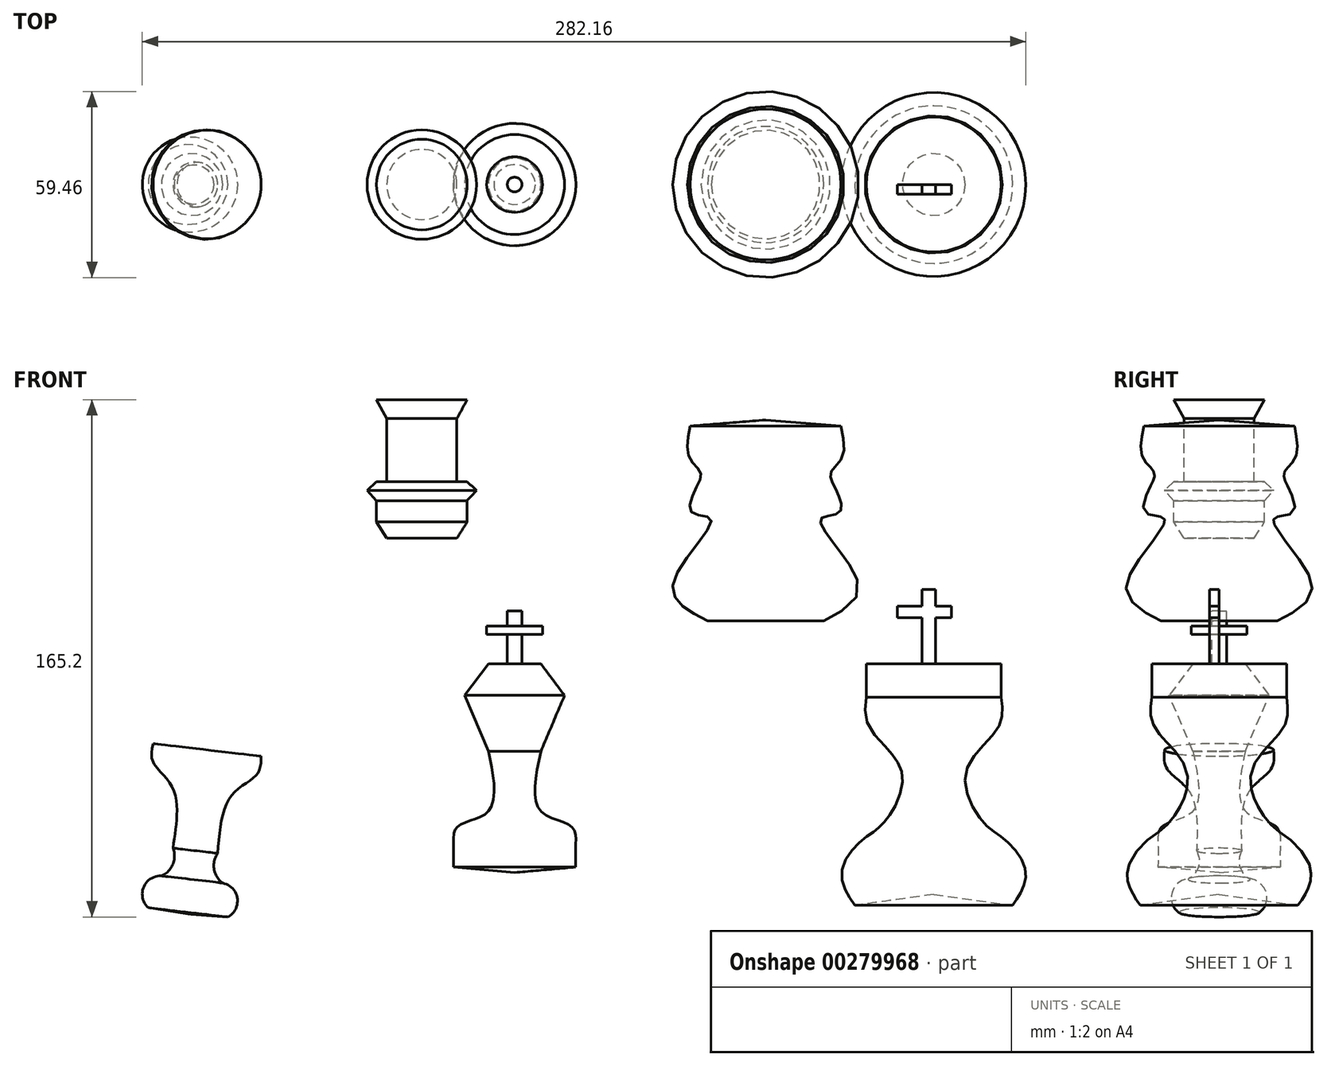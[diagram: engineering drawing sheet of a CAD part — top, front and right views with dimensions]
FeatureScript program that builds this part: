
annotation { "Feature Type Name" : "Feature", "Feature Type Description" : "" }
export const myFeature = defineFeature(function(context is Context, id is Id, definition is map)
    precondition{}
    {
        {
            var Q0;
            Q0=qCreatedBy(makeId("Front.planeOp"),FACE);
            var sketch = newSketch(context, id + "F0", { "sketchPlane" : qUnion([Q0])});
            skFitSpline(sketch, "E0", {"points": [v(-36.24, -64.9) * mm, v(-36.24, -57.78) * mm, v(-34.9, -51.99) * mm, v(-25.1, -47.08) * mm, v(-25.1, -27.92) * mm], "startDerivative": vector(0.5, 34) * mm, "endDerivative": vector(-14.24, 68.29) * mm});
            skLineSegment(sketch, "E1", {"start": v(-25.1, -27.92) * mm, "end": v(-32.67, -10.1) * mm});
            skLineSegment(sketch, "E2", {"start": v(-32.67, -10.1) * mm, "end": v(-25.1, 0) * mm});
            skLineSegment(sketch, "E3", {"start": v(-25.1, 0) * mm, "end": v(-16.72, 0) * mm});
            skLineSegment(sketch, "E4", {"start": v(-16.72, 0) * mm, "end": v(-16.72, -66.68) * mm});
            skLineSegment(sketch, "E5", {"start": v(-16.72, -66.68) * mm, "end": v(-36.2, -62.54) * mm});
            skLineSegment(sketch, "E6", {"start": v(-36.24, -64.9) * mm, "end": v(-16.72, -66.68) * mm});
            skLineSegment(sketch, "E7", {"start": v(-19.06, 0) * mm, "end": v(-19.06, 9.43) * mm});
            skLineSegment(sketch, "E8", {"start": v(-19.06, 9.43) * mm, "end": v(-25.62, 9.43) * mm});
            skLineSegment(sketch, "E9", {"start": v(-25.62, 9.43) * mm, "end": v(-25.62, 12.06) * mm});
            skLineSegment(sketch, "E10", {"start": v(-25.62, 12.06) * mm, "end": v(-19.06, 12.06) * mm});
            skLineSegment(sketch, "E11", {"start": v(-19.06, 12.06) * mm, "end": v(-19.06, 16.83) * mm});
            skLineSegment(sketch, "E12", {"start": v(-16.72, 0) * mm, "end": v(-16.72, 16.93) * mm});
            skLineSegment(sketch, "E13", {"start": v(-16.72, 16.93) * mm, "end": v(-19.06, 16.83) * mm});
            skSolve(sketch);
        }
        {
            var Q0;
            Q0=makeQuery(id+"F0.imprint","IMPRINT",FACE,{"disambiguationData":[TD([[makeQuery(id+"F0.imprint","IMPRINT",EDGE,{"derivedFrom":sQuery(id+"F0.wireOp",EDGE,"E0")}),-1.0]])]});
            var Q1;
            {var subQ0=sQuery(id+"F0.wireOp",EDGE,"E7");Q1=makeQuery(id+"F0.imprint","IMPRINT",FACE,{"disambiguationData":[TD([[makeQuery(id+"F0.imprint","IMPRINT",EDGE,{"derivedFrom":subQ0}),-1.0]])]});}
            var Q2;
            Q2=sQuery(id+"F0.wireOp",EDGE,"E4");
            revolve(context, id + "F1", {"entities" : qUnion([Q0, Q1]), "axis" : qUnion([Q2]), "revolveType" : RevolveType.FULL});
        }
        {
            var Q0;
            Q0=qCreatedBy(makeId("Front.planeOp"),FACE);
            var sketch = newSketch(context, id + "F2", { "sketchPlane" : qUnion([Q0])});
            skFitSpline(sketch, "E14", {"points": [v(91.97, -77.12) * mm, v(88.9, -72.13) * mm, v(88.08, -64.8) * mm, v(94.68, -55.93) * mm, v(101.12, -50.81) * mm, v(106.9, -34.61) * mm, v(96.49, -20.21) * mm, v(95.61, -10.61) * mm], "startDerivative": vector(-31.24, 43.9) * mm, "endDerivative": vector(10.25, 70.51) * mm});
            skLineSegment(sketch, "E15", {"start": v(95.61, -10.61) * mm, "end": v(95.61, 0) * mm});
            skLineSegment(sketch, "E16", {"start": v(95.61, 0) * mm, "end": v(117.13, 0) * mm});
            skLineSegment(sketch, "E17", {"start": v(117.13, 0) * mm, "end": v(117.13, -73.66) * mm});
            skLineSegment(sketch, "E18", {"start": v(117.13, -73.66) * mm, "end": v(91.97, -77.12) * mm});
            skSolve(sketch);
        }
        {
            var Q0;
            Q0=makeQuery(id+"F2.imprint","IMPRINT",FACE,{"disambiguationData":[TD([[makeQuery(id+"F2.imprint","IMPRINT",EDGE,{"derivedFrom":sQuery(id+"F2.wireOp",EDGE,"E14")}),-1.0]])]});
            var Q1;
            Q1=sQuery(id+"F2.wireOp",EDGE,"E17");
            revolve(context, id + "F3", {"entities" : qUnion([Q0]), "axis" : qUnion([Q1]), "revolveType" : RevolveType.FULL});
        }
        {
            var Q0;
            Q0=qCreatedBy(makeId("Front.planeOp"),FACE);
            var sketch = newSketch(context, id + "F4", { "sketchPlane" : qUnion([Q0])});
            skLineSegment(sketch, "E19", {"start": v(113.35, 0) * mm, "end": v(113.35, 14.69) * mm});
            skLineSegment(sketch, "E20", {"start": v(113.35, 14.69) * mm, "end": v(105.5, 14.69) * mm});
            skLineSegment(sketch, "E21", {"start": v(105.5, 18.43) * mm, "end": v(113.35, 18.43) * mm});
            skLineSegment(sketch, "E22", {"start": v(105.5, 18.43) * mm, "end": v(105.5, 14.69) * mm});
            skLineSegment(sketch, "E23", {"start": v(113.35, 18.43) * mm, "end": v(113.35, 23.7) * mm});
            skLineSegment(sketch, "E24", {"start": v(113.35, 23.7) * mm, "end": v(117.67, 23.7) * mm});
            skLineSegment(sketch, "E25", {"start": v(117.67, 23.7) * mm, "end": v(117.67, 0) * mm});
            skLineSegment(sketch, "E26", {"start": v(113.35, 18.43) * mm, "end": v(122.8, 18.43) * mm});
            skLineSegment(sketch, "E27", {"start": v(122.8, 18.43) * mm, "end": v(122.8, 14.69) * mm});
            skLineSegment(sketch, "E28", {"start": v(122.8, 14.69) * mm, "end": v(117.67, 14.69) * mm});
            skLineSegment(sketch, "E29", {"start": v(113.35, 0) * mm, "end": v(117.67, 0) * mm});
            skSolve(sketch);
        }
        {
            var Q0;
            Q0=makeQuery(id+"F4.imprint","IMPRINT",FACE,{"disambiguationData":[TD([[makeQuery(id+"F4.imprint","IMPRINT",EDGE,{"derivedFrom":sQuery(id+"F4.wireOp",EDGE,"E19")}),-1.0]])]});
            var Q1;
            {var subQ0=sQuery(id+"F4.wireOp",EDGE,"E23");Q1=makeQuery(id+"F4.imprint","IMPRINT",FACE,{"disambiguationData":[TD([[makeQuery(id+"F4.imprint","IMPRINT",EDGE,{"derivedFrom":subQ0}),-1.0]])]});}
            var Q2;
            {var subQ4=sQuery(id+"F4.wireOp",EDGE,"E27");Q2=makeQuery(id+"F4.imprint","IMPRINT",FACE,{"disambiguationData":[TD([[makeQuery(id+"F4.imprint","IMPRINT",EDGE,{"derivedFrom":subQ4}),-1.0]])]});}
            extrude(context, id + "F5", {"entities" : qUnion([Q0, Q1, Q2]), "operationType" : NewBodyOperationType.ADD, "depth" : 3.05 * mm});
        }
        {
            var Q0;
            Q0=qCreatedBy(makeId("Front.planeOp"),FACE);
            var sketch = newSketch(context, id + "F6", { "sketchPlane" : qUnion([Q0])});
            skArc(sketch, "E30", {"start": v(-129.56, -67.72) * mm, "mid": v(-135.2, -71.34) * mm, "end": v(-133.7, -77.87) * mm});
            skArc(sketch, "E31", {"start": v(-129.56, -67.72) * mm, "mid": v(-125.86, -64.06) * mm, "end": v(-125.82, -58.85) * mm});
            skFitSpline(sketch, "E32", {"points": [v(-125.82, -58.85) * mm, v(-125.82, -39.85) * mm, v(-132.17, -31.41) * mm, v(-132.17, -25.47) * mm], "startDerivative": vector(7.7, 49.05) * mm, "endDerivative": vector(5.43, 25) * mm});
            skLineSegment(sketch, "E33", {"start": v(-132.17, -25.47) * mm, "end": v(-114.9, -27.5) * mm});
            skLineSegment(sketch, "E34", {"start": v(-114.9, -27.5) * mm, "end": v(-121.04, -79.89) * mm});
            skLineSegment(sketch, "E35", {"start": v(-121.04, -79.89) * mm, "end": v(-133.7, -77.87) * mm});
            skSolve(sketch);
        }
        {
            var Q0;
            Q0=makeQuery(id+"F6.imprint","IMPRINT",FACE,{"disambiguationData":[TD([[makeQuery(id+"F6.imprint","IMPRINT",EDGE,{"derivedFrom":sQuery(id+"F6.wireOp",EDGE,"E30")}),1.0]])]});
            var Q1;
            Q1=sQuery(id+"F6.wireOp",EDGE,"E34");
            revolve(context, id + "F7", {"entities" : qUnion([Q0]), "axis" : qUnion([Q1]), "revolveType" : RevolveType.FULL});
        }
        {
            var Q0;
            Q0=qCreatedBy(makeId("Front.planeOp"),FACE);
            var sketch = newSketch(context, id + "F8", { "sketchPlane" : qUnion([Q0])});
            skLineSegment(sketch, "E36", {"start": v(-57, 40.11) * mm, "end": v(-35.15, 40.11) * mm});
            skLineSegment(sketch, "E37", {"start": v(-35.15, 40.11) * mm, "end": v(-31.87, 45.3) * mm});
            skLineSegment(sketch, "E38", {"start": v(-31.87, 45.3) * mm, "end": v(-31.87, 52.13) * mm});
            skLineSegment(sketch, "E39", {"start": v(-31.87, 52.13) * mm, "end": v(-28.86, 55.4) * mm});
            skLineSegment(sketch, "E40", {"start": v(-28.86, 55.4) * mm, "end": v(-31.87, 58.16) * mm});
            skLineSegment(sketch, "E41", {"start": v(-31.87, 58.16) * mm, "end": v(-35.15, 58.16) * mm});
            skLineSegment(sketch, "E42", {"start": v(-35.15, 58.16) * mm, "end": v(-35.15, 78.34) * mm});
            skLineSegment(sketch, "E43", {"start": v(-35.15, 78.34) * mm, "end": v(-31.87, 84.35) * mm});
            skLineSegment(sketch, "E44", {"start": v(-31.87, 84.35) * mm, "end": v(-46.34, 84.35) * mm});
            skLineSegment(sketch, "E45", {"start": v(-46.34, 84.35) * mm, "end": v(-46.34, 40.11) * mm});
            skSolve(sketch);
        }
        {
            var Q0;
            {var subQ0=sQuery(id+"F8.wireOp",EDGE,"E37");Q0=makeQuery(id+"F8.imprint","IMPRINT",FACE,{"disambiguationData":[TD([[makeQuery(id+"F8.imprint","IMPRINT",EDGE,{"derivedFrom":subQ0}),1.0]])]});}
            var Q1;
            Q1=sQuery(id+"F8.wireOp",EDGE,"E45");
            revolve(context, id + "F9", {"entities" : qUnion([Q0]), "axis" : qUnion([Q1]), "revolveType" : RevolveType.FULL});
        }
        {
            var Q0;
            Q0=qCreatedBy(makeId("Front.planeOp"),FACE);
            var sketch = newSketch(context, id + "F10", { "sketchPlane" : qUnion([Q0])});
            skFitSpline(sketch, "E46", {"points": [v(87.52, 75.95) * mm, v(87.8, 65.72) * mm, v(84.2, 61.01) * mm, v(85.86, 55.76) * mm, v(86.97, 48.29) * mm, v(80.88, 46.08) * mm, v(93.06, 25.6) * mm, v(82, 13.7) * mm], "startDerivative": vector(16, -79.46) * mm, "endDerivative": vector(-100.48, -51.29) * mm});
            skLineSegment(sketch, "E47", {"start": v(82, 13.7) * mm, "end": v(63.46, 13.7) * mm});
            skLineSegment(sketch, "E48", {"start": v(63.46, 13.7) * mm, "end": v(63.46, 77.89) * mm});
            skLineSegment(sketch, "E49", {"start": v(63.46, 77.89) * mm, "end": v(87.52, 75.95) * mm});
            skSolve(sketch);
        }
        {
            var Q0;
            Q0=makeQuery(id+"F10.imprint","IMPRINT",FACE,{"disambiguationData":[TD([[makeQuery(id+"F10.imprint","IMPRINT",EDGE,{"derivedFrom":sQuery(id+"F10.wireOp",EDGE,"E46")}),-1.0]])]});
            var Q1;
            Q1=sQuery(id+"F10.wireOp",EDGE,"E48");
            revolve(context, id + "F11", {"surfaceOperationType" : NewSurfaceOperationType.NEW, "entities" : qUnion([Q0]), "axis" : qUnion([Q1]), "revolveType" : RevolveType.FULL});
        }
    });
